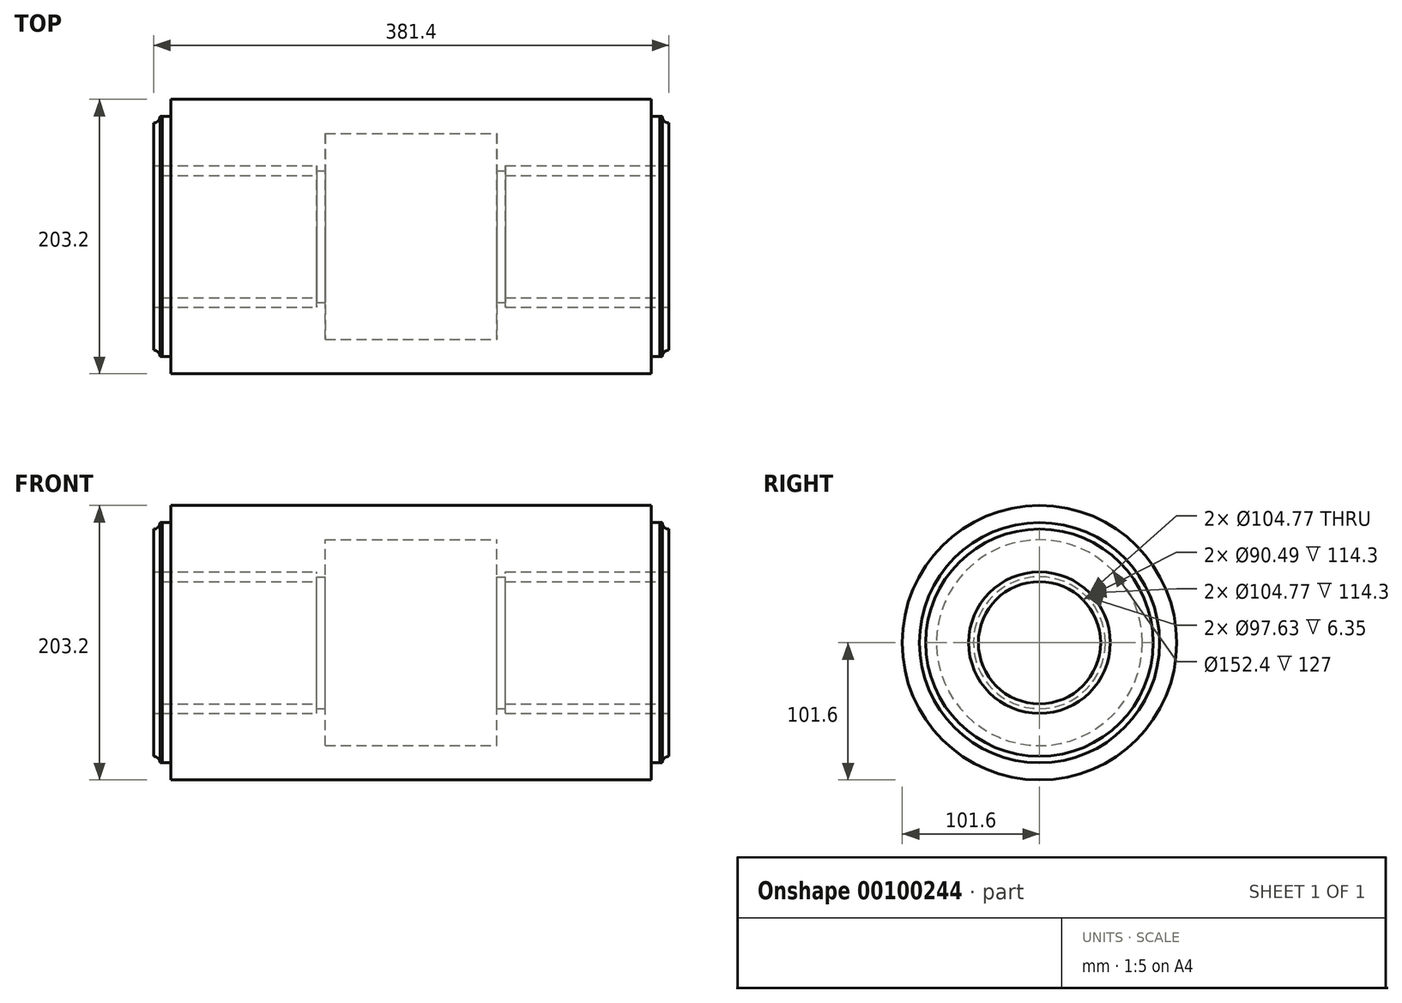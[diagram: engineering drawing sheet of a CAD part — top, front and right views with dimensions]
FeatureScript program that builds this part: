
annotation { "Feature Type Name" : "Feature", "Feature Type Description" : "" }
export const myFeature = defineFeature(function(context is Context, id is Id, definition is map)
    precondition{}
    {
        {
            var Q0;
            Q0=qCreatedBy(makeId("Front.planeOp"),FACE);
            var sketch = newSketch(context, id + "F0", { "sketchPlane" : qUnion([Q0])});
            skLineSegment(sketch, "E0", {"start": v(0, 0) * mm, "end": v(-341.84, 0) * mm, "construction": true});
            skLineSegment(sketch, "E1", {"start": v(-184.15, 45.24) * mm, "end": v(-184.15, 101.6) * mm});
            skLineSegment(sketch, "E2", {"start": v(-184.15, 101.6) * mm, "end": v(0, 101.6) * mm});
            skLineSegment(sketch, "E3", {"start": v(0, 0) * mm, "end": v(0, 149.6) * mm, "construction": true});
            skLineSegment(sketch, "E4", {"start": v(-184.15, 45.24) * mm, "end": v(-69.85, 45.24) * mm});
            skLineSegment(sketch, "E5", {"start": v(-184.15, 52.39) * mm, "end": v(-69.85, 52.39) * mm});
            skLineSegment(sketch, "E6", {"start": v(-69.85, 45.24) * mm, "end": v(-69.85, 52.39) * mm});
            skLineSegment(sketch, "E7", {"start": v(-69.85, 48.82) * mm, "end": v(-63.5, 48.82) * mm});
            skLineSegment(sketch, "E8", {"start": v(-63.5, 48.82) * mm, "end": v(-63.5, 76.2) * mm});
            skLineSegment(sketch, "E9", {"start": v(-63.5, 76.2) * mm, "end": v(0, 76.2) * mm});
            skLineSegment(sketch, "E10", {"start": v(-184.15, 101.6) * mm, "end": v(-190.7, 101.6) * mm});
            skLineSegment(sketch, "E11", {"start": v(-184.15, 52.39) * mm, "end": v(-190.7, 52.39) * mm});
            skLineSegment(sketch, "E12", {"start": v(-190.7, 52.39) * mm, "end": v(-190.7, 101.6) * mm});
            skLineSegment(sketch, "E13", {"start": v(-177.8, 101.6) * mm, "end": v(-177.8, 88.9) * mm});
            skLineSegment(sketch, "E14", {"start": v(-177.8, 88.9) * mm, "end": v(-190.7, 88.9) * mm});
            skLineSegment(sketch, "E15.MirrorCS", {"start": v(69.85, 45.24) * mm, "end": v(69.85, 52.39) * mm});
            skLineSegment(sketch, "E16.MirrorCS", {"start": v(69.85, 48.82) * mm, "end": v(63.5, 48.82) * mm});
            skLineSegment(sketch, "E17.MirrorCS", {"start": v(184.15, 101.6) * mm, "end": v(190.7, 101.6) * mm});
            skLineSegment(sketch, "E18.MirrorCS", {"start": v(184.15, 52.39) * mm, "end": v(190.7, 52.39) * mm});
            skLineSegment(sketch, "E19.MirrorCS", {"start": v(177.8, 88.9) * mm, "end": v(190.7, 88.9) * mm});
            skLineSegment(sketch, "E20.MirrorCS", {"start": v(63.5, 76.2) * mm, "end": v(0, 76.2) * mm});
            skLineSegment(sketch, "E21.MirrorCS", {"start": v(177.8, 101.6) * mm, "end": v(177.8, 88.9) * mm});
            skLineSegment(sketch, "E22.MirrorCS", {"start": v(184.15, 45.24) * mm, "end": v(69.85, 45.24) * mm});
            skLineSegment(sketch, "E23.MirrorCS", {"start": v(63.5, 48.82) * mm, "end": v(63.5, 76.2) * mm});
            skLineSegment(sketch, "E24.MirrorCS", {"start": v(184.15, 101.6) * mm, "end": v(0, 101.6) * mm});
            skLineSegment(sketch, "E25.MirrorCS", {"start": v(190.7, 52.39) * mm, "end": v(190.7, 101.6) * mm});
            skLineSegment(sketch, "E26.MirrorCS", {"start": v(184.15, 45.24) * mm, "end": v(184.15, 101.6) * mm});
            skLineSegment(sketch, "E27.MirrorCS", {"start": v(184.15, 52.39) * mm, "end": v(69.85, 52.39) * mm});
            skArc(sketch, "E28", {"start": v(-190.7, 84.14) * mm, "mid": v(-187.34, 85.53) * mm, "end": v(-185.94, 88.9) * mm});
            skArc(sketch, "E29.MirrorCS", {"start": v(190.7, 84.14) * mm, "mid": v(187.34, 85.53) * mm, "end": v(185.94, 88.9) * mm});
            skSolve(sketch);
        }
        {
            var Q0;
            {var subQ12=sQuery(id+"F0.wireOp",EDGE,"E5");Q0=makeQuery(id+"F0.imprint","IMPRINT",FACE,{"disambiguationData":[TD([[makeQuery(id+"F0.imprint","IMPRINT",EDGE,{"derivedFrom":subQ12}),1.0]])]});}
            var Q1;
            Q1=sQuery(id+"F0.wireOp",EDGE,"E0");
            revolve(context, id + "F1", {"entities" : qUnion([Q0]), "axis" : qUnion([Q1]), "revolveType" : RevolveType.FULL});
        }
        {
            var Q0;
            {var subQ1=sQuery(id+"F0.wireOp",EDGE,"E4");Q0=makeQuery(id+"F0.imprint","IMPRINT",FACE,{"disambiguationData":[TD([[makeQuery(id+"F0.imprint","IMPRINT",EDGE,{"derivedFrom":subQ1}),1.0]])]});}
            var Q1;
            {var subQ0=sQuery(id+"F0.wireOp",EDGE,"E11");Q1=makeQuery(id+"F0.imprint","IMPRINT",FACE,{"disambiguationData":[TD([[makeQuery(id+"F0.imprint","IMPRINT",EDGE,{"derivedFrom":subQ0}),-1.0]])]});}
            var Q2;
            {var subQ0=sQuery(id+"F0.wireOp",EDGE,"E22.MirrorCS");Q2=makeQuery(id+"F0.imprint","IMPRINT",FACE,{"disambiguationData":[TD([[makeQuery(id+"F0.imprint","IMPRINT",EDGE,{"derivedFrom":subQ0}),-1.0]])]});}
            var Q3;
            {var subQ0=sQuery(id+"F0.wireOp",EDGE,"E18.MirrorCS");Q3=makeQuery(id+"F0.imprint","IMPRINT",FACE,{"disambiguationData":[TD([[makeQuery(id+"F0.imprint","IMPRINT",EDGE,{"derivedFrom":subQ0}),1.0]])]});}
            var Q4;
            Q4=sQuery(id+"F0.wireOp",EDGE,"E0");
            revolve(context, id + "F2", {"entities" : qUnion([Q0, Q1, Q2, Q3]), "axis" : qUnion([Q4]), "revolveType" : RevolveType.FULL});
        }
    });
